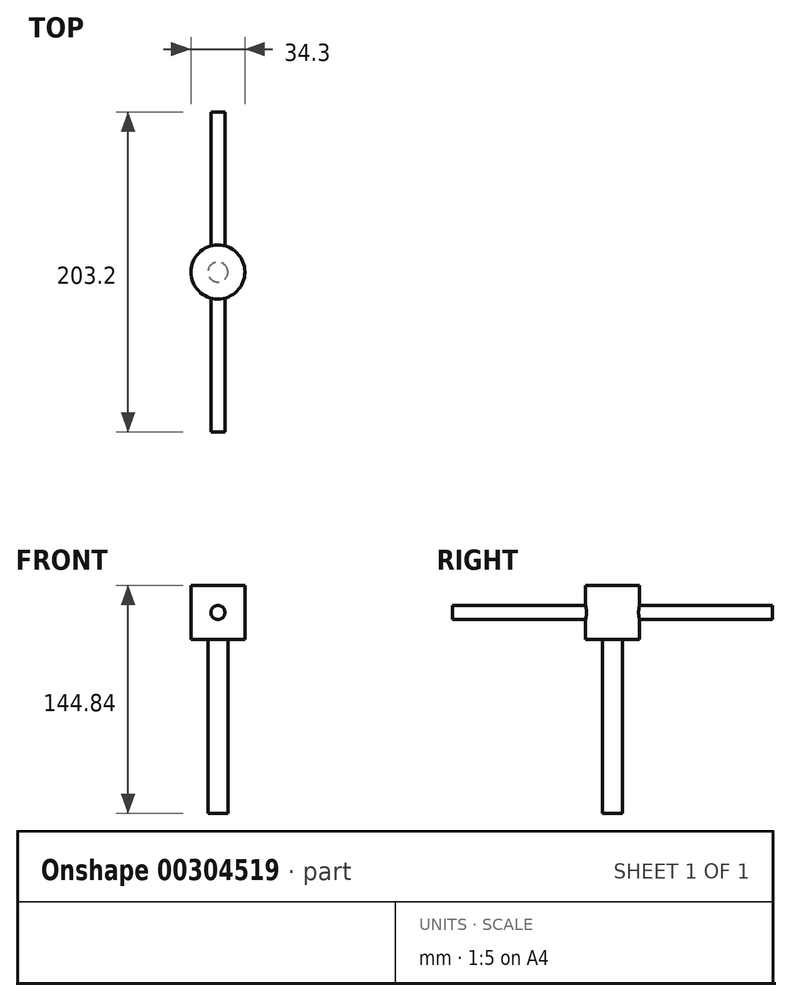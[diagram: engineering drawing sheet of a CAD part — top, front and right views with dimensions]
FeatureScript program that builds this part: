
annotation { "Feature Type Name" : "Feature", "Feature Type Description" : "" }
export const myFeature = defineFeature(function(context is Context, id is Id, definition is map)
    precondition{}
    {
        {
            var Q0;
            Q0=qCreatedBy(makeId("Top.planeOp"),FACE);
            var sketch = newSketch(context, id + "F0", { "sketchPlane" : qUnion([Q0])});
            skCircle(sketch, "E0", {"center": v(0, 0) * mm, "radius": 17.15 * mm});
            skSolve(sketch);
        }
        {
            var Q0;
            Q0=makeQuery(id+"F0.imprint","IMPRINT",FACE,{"disambiguationData":[TD([[makeQuery(id+"F0.imprint","IMPRINT",EDGE,{"derivedFrom":sQuery(id+"F0.wireOp",EDGE,"E0")}),1.0]])]});
            extrude(context, id + "F1", {"entities" : qUnion([Q0]), "endBound" : BoundingType.SYMMETRIC, "depth" : 34.3 * mm});
        }
        {
            var Q0;
            Q0=qCreatedBy(makeId("Front.planeOp"),FACE);
            var sketch = newSketch(context, id + "F2", { "sketchPlane" : qUnion([Q0])});
            skLineSegment(sketch, "E1", {"start": v(0, 0) * mm, "end": v(0, -152.16) * mm, "construction": true});
            skLineSegment(sketch, "E2", {"start": v(0, -17.15) * mm, "end": v(-6.35, -17.15) * mm});
            skLineSegment(sketch, "E3", {"start": v(-6.35, -17.15) * mm, "end": v(-6.35, -127.69) * mm});
            skLineSegment(sketch, "E4", {"start": v(-6.35, -127.69) * mm, "end": v(0, -127.69) * mm});
            skLineSegment(sketch, "E5", {"start": v(0, -127.69) * mm, "end": v(0, -17.15) * mm});
            skSolve(sketch);
        }
        {
            var Q0;
            Q0=makeQuery(id+"F2.imprint","IMPRINT",FACE,{"disambiguationData":[TD([[makeQuery(id+"F2.imprint","IMPRINT",EDGE,{"derivedFrom":sQuery(id+"F2.wireOp",EDGE,"E2")}),1.0]])]});
            var Q1;
            Q1=sQuery(id+"F2.wireOp",EDGE,"E1");
            revolve(context, id + "F3", {"operationType" : NewBodyOperationType.ADD, "entities" : qUnion([Q0]), "axis" : qUnion([Q1]), "revolveType" : RevolveType.FULL});
        }
        {
            var Q0;
            Q0=qCreatedBy(makeId("Front.planeOp"),FACE);
            var sketch = newSketch(context, id + "F4", { "sketchPlane" : qUnion([Q0])});
            skCircle(sketch, "E6", {"center": v(0, 0) * mm, "radius": 4.45 * mm});
            skSolve(sketch);
        }
        {
            var Q0;
            Q0 = qSketchRegion(id + "F4", true);
            extrude(context, id + "F5", {"entities" : qUnion([Q0]), "operationType" : NewBodyOperationType.REMOVE, "endBound" : BoundingType.THROUGH_ALL, "oppositeDirection" : true, "depth" : 31.75 * mm, "hasSecondDirection" : true, "secondDirectionOppositeDirection" : false, "secondDirectionDepth" : 25.4 * mm});
        }
        {
            var Q0;
            Q0=qCreatedBy(makeId("Front.planeOp"),FACE);
            var sketch = newSketch(context, id + "F6", { "sketchPlane" : qUnion([Q0])});
            skCircle(sketch, "E7", {"center": v(0, 0) * mm, "radius": 4.44 * mm});
            skSolve(sketch);
        }
        {
            var Q0;
            Q0 = qSketchRegion(id + "F6", true);
            extrude(context, id + "F7", {"entities" : qUnion([Q0]), "operationType" : NewBodyOperationType.ADD, "endBound" : BoundingType.SYMMETRIC, "depth" : 203.2 * mm});
        }
    });
